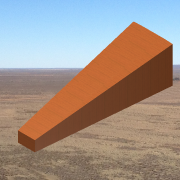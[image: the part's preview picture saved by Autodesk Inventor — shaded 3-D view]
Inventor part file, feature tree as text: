
AUTODESK INVENTOR PART (.ipt)
format: ipt  version: 2014 SP1 (Build 180222100, 222)  size: 141,824 bytes
history: native  units: in
note: dims shown in document units (in); Inventor stores cm internally (conversion verified against a paired STEP export)
features: sketch x3, revolve x2, extrude x1
ambient origin geometry x8: Origin, YZ Plane, XZ Plane, XY Plane, X Axis, Y Axis, Z Axis, Center Point
bodies: Solid1 (feature_tree)
feature tree (6):
  extrude  "Extrusion1"  Depth=17.0in
  revolve  "Revolution1"  [1 undecoded]
  revolve  "Revolution2"  [1 undecoded]
  sketch  "Sketch1"  dims[d0=60.0in d1=17.0in]
  sketch  "Sketch2"  dims[d2=5.0in d3=8.0in d4=0.0in]
  sketch  "Sketch3"  dims[d5=0.0344in d6=0.0344in]
note: 2 required parameter values undecoded (feature->parameter linkage not recoverable at this tier; creation-order binding heuristic only, values carry confidence <= 0.55)
